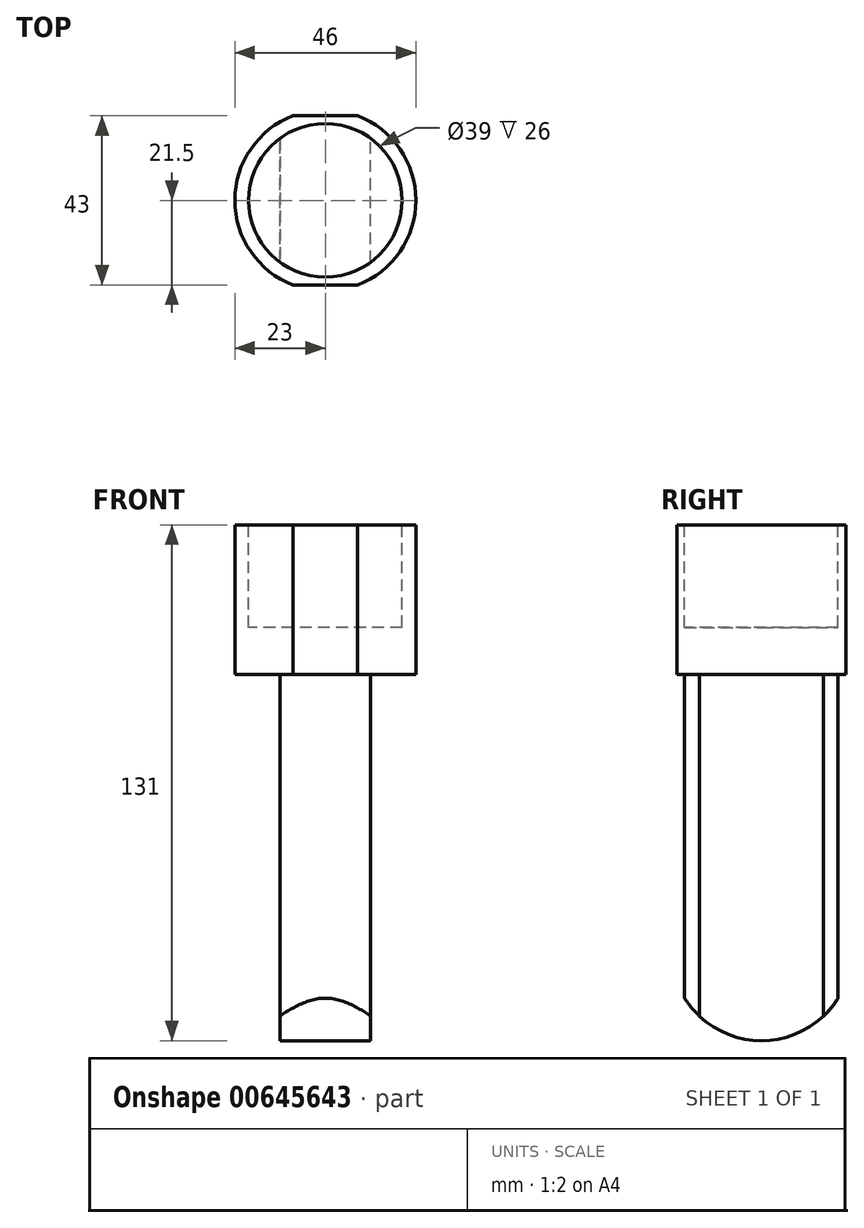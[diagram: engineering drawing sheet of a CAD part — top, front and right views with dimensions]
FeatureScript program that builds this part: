
annotation { "Feature Type Name" : "Feature", "Feature Type Description" : "" }
export const myFeature = defineFeature(function(context is Context, id is Id, definition is map)
    precondition{}
    {
        {
            var Q0;
            Q0=qCreatedBy(makeId("Top.planeOp"),FACE);
            var sketch = newSketch(context, id + "F0", { "sketchPlane" : qUnion([Q0])});
            skArc(sketch, "E0", {"start": v(-8.17, 21.5) * mm, "mid": v(-23, 0) * mm, "end": v(-8.17, -21.5) * mm});
            skLineSegment(sketch, "E1", {"start": v(-8.17, 21.5) * mm, "end": v(8.17, 21.5) * mm});
            skLineSegment(sketch, "E2.MirrorCS", {"start": v(-8.17, -21.5) * mm, "end": v(8.17, -21.5) * mm});
            skArc(sketch, "E3.trimOffspring", {"start": v(8.17, -21.5) * mm, "mid": v(23, 0) * mm, "end": v(8.17, 21.5) * mm});
            skSolve(sketch);
        }
        {
            var Q0;
            Q0=makeQuery(id+"F0.imprint","IMPRINT",FACE,{"disambiguationData":[TD([[makeQuery(id+"F0.imprint","IMPRINT",EDGE,{"derivedFrom":sQuery(id+"F0.wireOp",EDGE,"E0")}),1.0]])]});
            extrude(context, id + "F1", {"entities" : qUnion([Q0]), "depth" : 38 * mm, "offsetDistance" : 25 * mm});
        }
        {
            var Q0;
            Q0=makeQuery(id+"F1.opExtrude","CAP_FACE",FACE,{"disambiguationData":[OSD([sQuery(id+"F0.wireOp",EDGE,"E0"),sQuery(id+"F0.wireOp",EDGE,"E1"),sQuery(id+"F0.wireOp",EDGE,"E2.MirrorCS"),sQuery(id+"F0.wireOp",EDGE,"E3.trimOffspring")])],"isStart":false});
            var sketch = newSketch(context, id + "F2", { "sketchPlane" : qUnion([Q0])});
            skCircle(sketch, "E4", {"center": v(0, 0) * mm, "radius": 19.5 * mm});
            skSolve(sketch);
        }
        {
            var Q0;
            Q0=makeQuery(id+"F2.imprint","IMPRINT",FACE,{"disambiguationData":[TD([[makeQuery(id+"F2.imprint","IMPRINT",EDGE,{"derivedFrom":sQuery(id+"F2.wireOp",EDGE,"E4")}),1.0]])]});
            extrude(context, id + "F3", {"entities" : qUnion([Q0]), "operationType" : NewBodyOperationType.REMOVE, "oppositeDirection" : true, "depth" : 26 * mm, "offsetDistance" : 25 * mm});
        }
        {
            var Q0;
            Q0=makeQuery(id+"F1.opExtrude","CAP_FACE",FACE,{"disambiguationData":[OSD([sQuery(id+"F0.wireOp",EDGE,"E0"),sQuery(id+"F0.wireOp",EDGE,"E1"),sQuery(id+"F0.wireOp",EDGE,"E2.MirrorCS"),sQuery(id+"F0.wireOp",EDGE,"E3.trimOffspring")])],"isStart":true});
            var sketch = newSketch(context, id + "F4", { "sketchPlane" : qUnion([Q0])});
            skArc(sketch, "E5", {"start": v(-11.5, -15.75) * mm, "mid": v(0, -19.5) * mm, "end": v(11.5, -15.75) * mm});
            skLineSegment(sketch, "E6", {"start": v(-11.5, 15.75) * mm, "end": v(-11.5, -15.75) * mm});
            skLineSegment(sketch, "E7.MirrorCS", {"start": v(11.5, 15.75) * mm, "end": v(11.5, -15.75) * mm});
            skArc(sketch, "E8.trimOffspring", {"start": v(11.5, 15.75) * mm, "mid": v(0, 19.5) * mm, "end": v(-11.5, 15.75) * mm});
            skSolve(sketch);
        }
        {
            var Q0;
            Q0=makeQuery(id+"F4.imprint","IMPRINT",FACE,{"disambiguationData":[TD([[makeQuery(id+"F4.imprint","IMPRINT",EDGE,{"derivedFrom":sQuery(id+"F4.wireOp",EDGE,"E5")}),1.0]])]});
            extrude(context, id + "F5", {"entities" : qUnion([Q0]), "operationType" : NewBodyOperationType.ADD, "depth" : 93 * mm, "offsetDistance" : 25 * mm});
        }
        {
            var Q0;
            Q0=makeQuery(id+"F5.opExtrude","SWEPT_FACE",FACE,{"disambiguationData":[OSD([sQuery(id+"F4.wireOp",EDGE,"E6")])]});
            var sketch = newSketch(context, id + "F6", { "sketchPlane" : qUnion([Q0])});
            skPoint(sketch, "E9", {"position": v(0, -70) * mm});
            skCircle(sketch, "E10", {"center": v(0, -70) * mm, "radius": 23 * mm});
            skLineSegment(sketch, "E11", {"start": v(-19.63, -81.98) * mm, "end": v(-36.67, -101.66) * mm});
            skLineSegment(sketch, "E12", {"start": v(-36.67, -101.66) * mm, "end": v(38.12, -101.66) * mm});
            skLineSegment(sketch, "E13", {"start": v(38.12, -101.66) * mm, "end": v(19.47, -82.24) * mm});
            skSolve(sketch);
        }
        {
            var Q0;
            {var subQ5=sQuery(id+"F6.wireOp",EDGE,"E11");Q0=makeQuery(id+"F6.imprint","IMPRINT",FACE,{"disambiguationData":[TD([[makeQuery(id+"F6.imprint","IMPRINT",EDGE,{"derivedFrom":subQ5}),1.0]])]});}
            var Q1;
            {var subQ0=sQuery(id+"F6.wireOp",EDGE,"E10");var subQ1=sQuery(id+"F4.wireOp",EDGE,"E6");var subQ4=makeQuery(id+"F5.opExtrude","CAP_EDGE",EDGE,{"disambiguationData":[OSD([subQ1])],"isStart":false});var subQ5=makeQuery(id+"F6.imprint","INTERSECT",VERTEX,{"derivedFrom":[subQ4,subQ0]});Q1=makeQuery(id+"F6.imprint","IMPRINT",FACE,{"disambiguationData":[TD([[makeQuery(id+"F6.imprint","IMPRINT",EDGE,{"disambiguationData":[TD([[subQ5,1.0]])],"derivedFrom":subQ0}),-1.0]])]});}
            var Q2;
            {var subQ0=sQuery(id+"F6.wireOp",EDGE,"E10");var subQ1=sQuery(id+"F4.wireOp",EDGE,"E6");var subQ2=makeQuery(id+"F5.opExtrude","CAP_EDGE",EDGE,{"disambiguationData":[OSD([subQ1])],"isStart":false});var subQ3=makeQuery(id+"F6.imprint","INTERSECT",VERTEX,{"derivedFrom":[subQ2,subQ0]});Q2=makeQuery(id+"F6.imprint","IMPRINT",FACE,{"disambiguationData":[TD([[makeQuery(id+"F6.imprint","IMPRINT",EDGE,{"disambiguationData":[TD([[subQ3,-1.0]])],"derivedFrom":subQ0}),-1.0]])]});}
            extrude(context, id + "F7", {"entities" : qUnion([Q0, Q1, Q2]), "operationType" : NewBodyOperationType.REMOVE, "endBound" : BoundingType.THROUGH_ALL, "oppositeDirection" : true, "depth" : 25 * mm, "offsetDistance" : 25 * mm});
        }
    });
